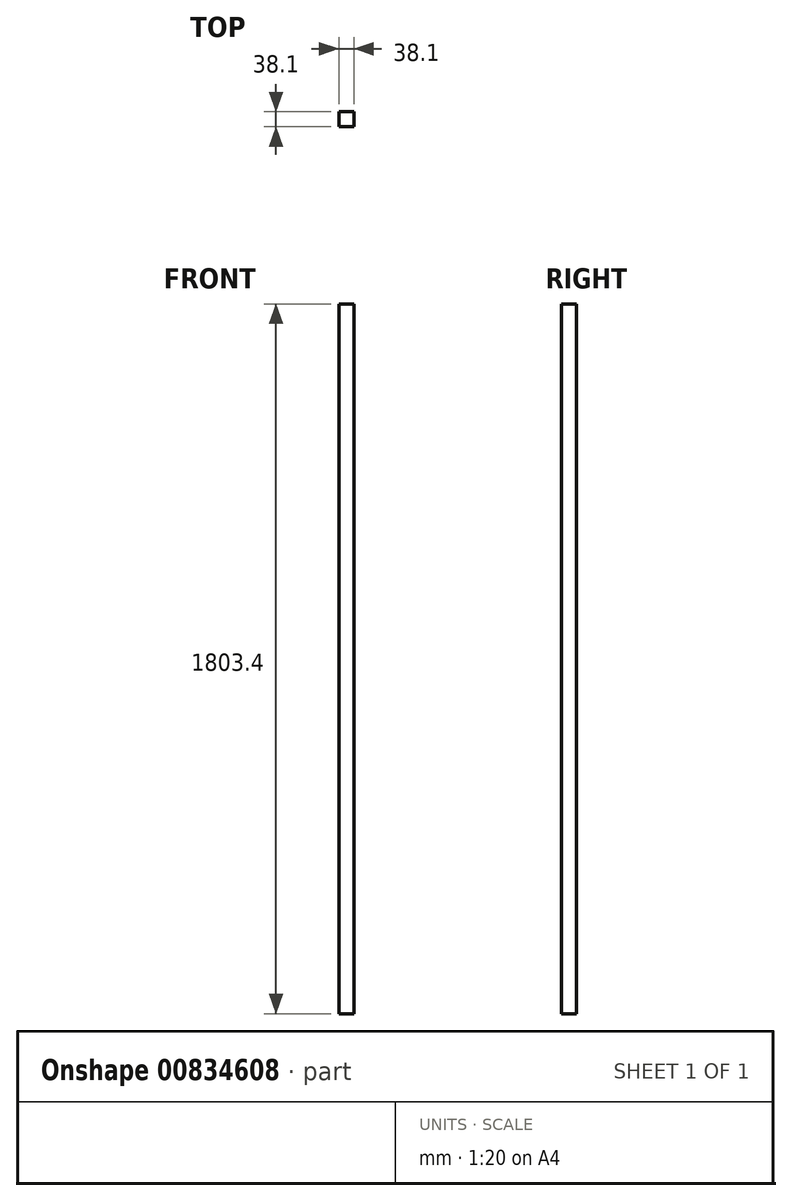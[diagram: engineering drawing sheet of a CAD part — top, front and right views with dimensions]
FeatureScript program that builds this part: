
annotation { "Feature Type Name" : "Feature", "Feature Type Description" : "" }
export const myFeature = defineFeature(function(context is Context, id is Id, definition is map)
    precondition{}
    {
        {
            var Q0;
            Q0=qCreatedBy(makeId("Top.planeOp"),FACE);
            var sketch = newSketch(context, id + "F0", { "sketchPlane" : qUnion([Q0])});
            skLineSegment(sketch, "E0.bottom", {"start": v(19.05, 19.05) * mm, "end": v(-19.05, 19.05) * mm});
            skLineSegment(sketch, "E0.top", {"start": v(19.05, -19.05) * mm, "end": v(-19.05, -19.05) * mm});
            skLineSegment(sketch, "E0.left", {"start": v(19.05, 19.05) * mm, "end": v(19.05, -19.05) * mm});
            skLineSegment(sketch, "E0.right", {"start": v(-19.05, 19.05) * mm, "end": v(-19.05, -19.05) * mm});
            skPoint(sketch, "E0.middle", {"position": v(0, 0) * mm});
            skSolve(sketch);
        }
        {
            var Q0;
            Q0 = qSketchRegion(id + "F0", true);
            extrude(context, id + "F1", {"entities" : qUnion([Q0]), "oppositeDirection" : true, "depth" : 1803.4 * mm, "offsetDistance" : 25.4 * mm});
        }
    });
